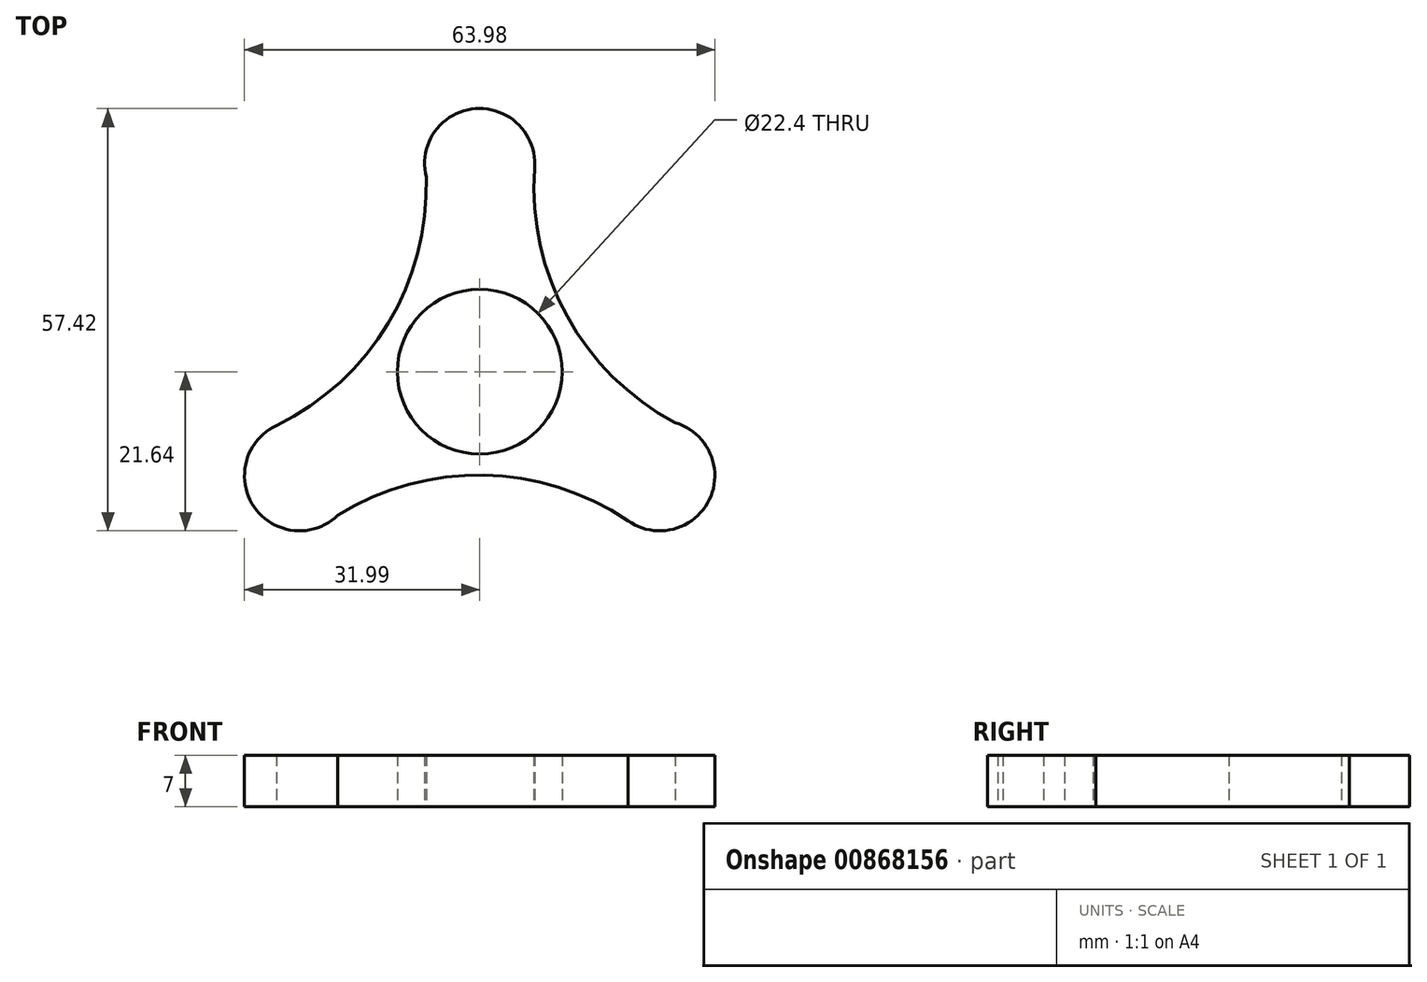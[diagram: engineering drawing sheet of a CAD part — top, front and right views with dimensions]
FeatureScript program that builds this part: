
annotation { "Feature Type Name" : "Feature", "Feature Type Description" : "" }
export const myFeature = defineFeature(function(context is Context, id is Id, definition is map)
    precondition{}
    {
        {
            var Q0;
            Q0=qCreatedBy(makeId("Top.planeOp"),FACE);
            var sketch = newSketch(context, id + "F0", { "sketchPlane" : qUnion([Q0])});
            skCircle(sketch, "E0", {"center": v(0, 0) * mm, "radius": 11.2 * mm});
            skArc(sketch, "E1", {"start": v(7.47, 27.59) * mm, "mid": v(-0.57, 35.76) * mm, "end": v(-7.28, 26.47) * mm});
            skArc(sketch, "E2.1.0", {"start": v(-27.63, -7.33) * mm, "mid": v(-30.68, -18.37) * mm, "end": v(-19.29, -19.54) * mm});
            skArc(sketch, "E2.2.0", {"start": v(20.16, -20.26) * mm, "mid": v(31.25, -17.39) * mm, "end": v(26.57, -6.93) * mm});
            skArc(sketch, "E3", {"start": v(-27.87, -7.44) * mm, "mid": v(-11.87, 7.57) * mm, "end": v(-7.46, 29.06) * mm});
            skArc(sketch, "E4.1.0", {"start": v(20.38, -20.41) * mm, "mid": v(-0.62, -14.06) * mm, "end": v(-21.44, -20.99) * mm});
            skArc(sketch, "E4.2.0", {"start": v(7.49, 27.86) * mm, "mid": v(12.49, 6.5) * mm, "end": v(28.9, -8.07) * mm});
            skSolve(sketch);
        }
        {
            var Q0;
            Q0 = qSketchRegion(id + "F0", true);
            extrude(context, id + "F1", {"entities" : qUnion([Q0]), "depth" : 7 * mm, "offsetDistance" : 25 * mm});
        }
    });
